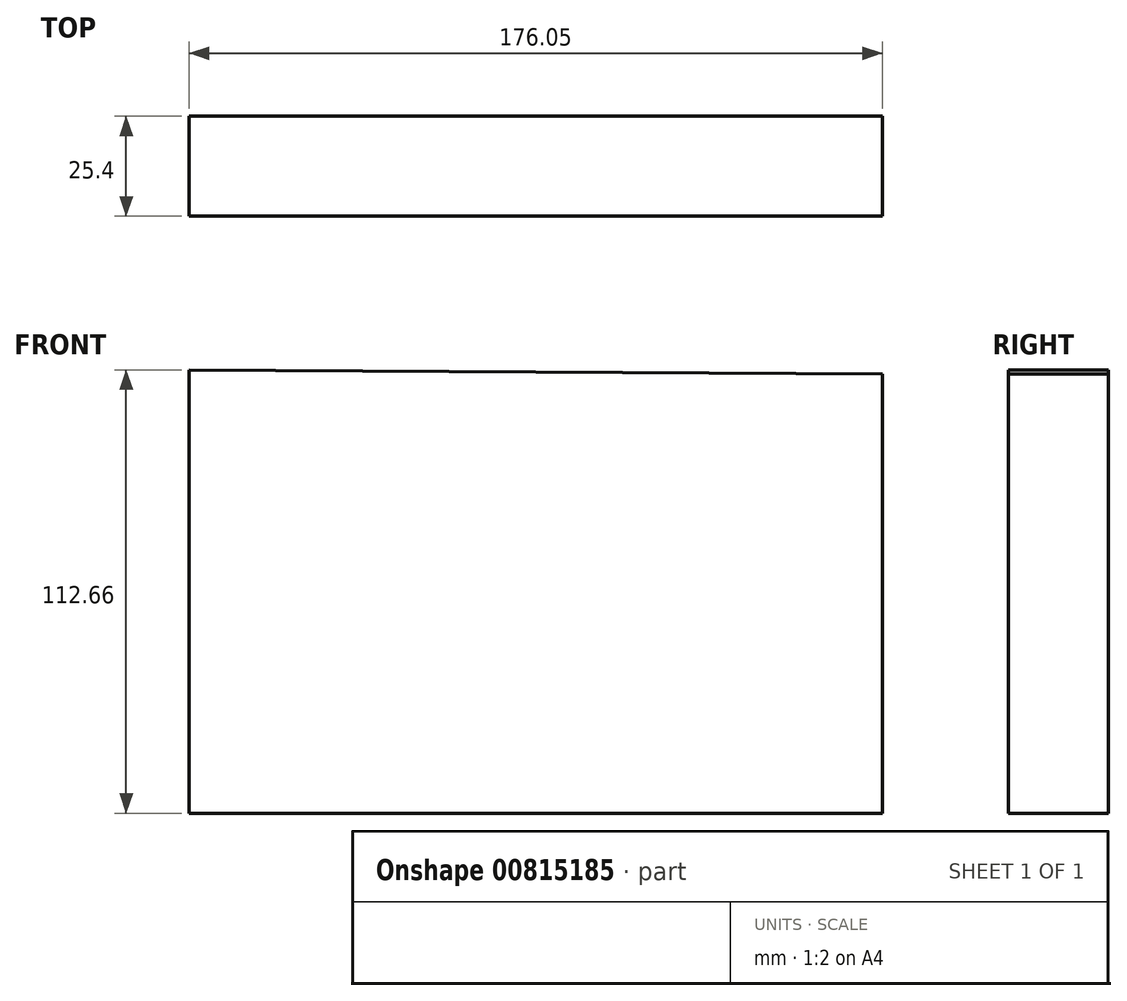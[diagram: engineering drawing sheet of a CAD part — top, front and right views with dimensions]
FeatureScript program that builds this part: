
annotation { "Feature Type Name" : "Feature", "Feature Type Description" : "" }
export const myFeature = defineFeature(function(context is Context, id is Id, definition is map)
    precondition{}
    {
        {
            var Q0;
            Q0=qCreatedBy(makeId("Front.planeOp"),FACE);
            var sketch = newSketch(context, id + "F0", { "sketchPlane" : qUnion([Q0])});
            skLineSegment(sketch, "E0", {"start": v(-75.92, 50.73) * mm, "end": v(-75.92, -61.93) * mm});
            skLineSegment(sketch, "E1", {"start": v(-75.92, -61.93) * mm, "end": v(100.13, -61.93) * mm});
            skLineSegment(sketch, "E2", {"start": v(100.13, -61.93) * mm, "end": v(100.13, 49.66) * mm});
            skLineSegment(sketch, "E3", {"start": v(100.13, 49.66) * mm, "end": v(-75.92, 50.73) * mm});
            skSolve(sketch);
        }
        {
            var Q0;
            Q0=makeQuery(id+"F0.imprint","IMPRINT",FACE,{"disambiguationData":[TD([[makeQuery(id+"F0.imprint","IMPRINT",EDGE,{"derivedFrom":sQuery(id+"F0.wireOp",EDGE,"E0")}),1.0]])]});
            extrude(context, id + "F1", {"entities" : qUnion([Q0]), "depth" : 25.4 * mm, "offsetDistance" : 25.4 * mm});
        }
    });
